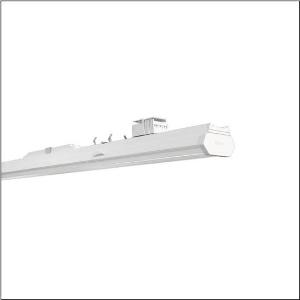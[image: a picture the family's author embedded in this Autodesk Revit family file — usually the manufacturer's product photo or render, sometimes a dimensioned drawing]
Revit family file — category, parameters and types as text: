
# Revit family: licross_11_protected_mo_51tp12dn495gd
name_source: partatom
category: Lighting Fixtures
units: mm (PartAtom-declared; Revit-internal decimal feet)

## family parameters
Cut with Voids When Loaded = No
Host = Face
Light Source = No
Part Type = Normal
Room Calculation Point = No
Round Connector Dimension = Use Diameter
Shared = No

## types (1)
- --- (1 x LED, 1500 lm, 9.3 W, 4000K)
    Apparent Load = 9 VA
    CIE Flux Codes = 73 92 98 99 100
    Color Rendering = 80
    Color Temperature = 4000K
    Default Elevation = 1800 mm
    Description = Licross 11 Protected MO, luminaire insert, of sheet steel, galvanised, coil coated, white, length: 1.500mm, width: 90mm, height: 101mm, LED rated luminous flux: 9.980lm, light colour: 840, SDCM (Standard Deviation of Colour Matching)MacAdam ≤ 2 SDCM (initial), control gear: DALI 2 (for two DALI lines), with plug, 6-pole, with phase selection, mains connection: 220..240V, AC/DC, 0/50..60Hz, rated input power: 57W, internal wiring halogen-free, for central battery installations according to EN 60598-2-22, for emergency light function, without changeover relay, primary optical cover: cover, of PMMA, light emission: direct distribution, primary light characteristic: symmetric, protection rating (complete): IP64, insulation class (complete): insulation class I (protective earthing), certification: CE, ENEC, VDE, UKCA, protection symbol: D if used in an environment with conductive dust loads with corresponding accessories, impact resistance: IK06, permissible ambient temperature for indoor applications: -25..+35°C, standard: EN 60598-2-22, corresponds to IFS (International Featured Standards) requirements for safety and quality in the food industry, reducing of maximum allowable ambient temperature of 5°C with ceiling mounting, LABS conformity tested according to VDMA 24364:2018-05, The light source and the operating device comply with the requirements of the Ecodesign Regulation (EU) 2019/2020 and are replaceable in accordance with this regulation, packaging unit: 1 piece
    Height = 92 mm
    Lamp = 1 x LED
    Lamp Light Flux = 1500 lm
    Lamp Power = 9.3 W
    Lamp count = 1
    Length = 1500 mm  [stored 4.92126 ft]
    Luminous efficacy = 161 lm/W
    Manufacturer = Siteco
    ModVariant = No
    Model = 51TP12DN495GD
    Mounting Place = Ceiling
    Mounting Type = Pendant
    Number of Poles = 1
    OnlyDefault = Yes
    Power Factor = 1
    Product Name = Licross 11 Protected MO
    Product group = luminaire insert | ceiling pendant
    ProductGroupID = 901
    Protection Class = Protection class I
    Protection Degree = IP 64
    RLX_Detail_Level = 1
    RLX_Emergency_Light_Flux = 0 lm
    RLX_Emergency_Type = 0
    RLX_Emergency_Type_DB = No
    RlxData = <blob elided: 25169 chars, md5=a519cff8>
    Socket = socket
    Standby Power = 0 W
    System Light Flux = 1500 lm
    System Power = 9 W
    Type Comments = : DC mode (central or group accumulator) initial emergency light level
    Type Image = l_1256148.jpg
    URL = http://relux.com
    VarID = @adj_093129
    Voltage = 0 V
    Weight = 0.00 kg
    Width = 88 mm

note: [stored X ft] marks values corroborated as IEEE doubles in the binary element streams (Revit-internal decimal feet)

## geometry (parser evidence)
native form markers: Blend x4, Sweep x10
no freeform markers — native parametric forms only
